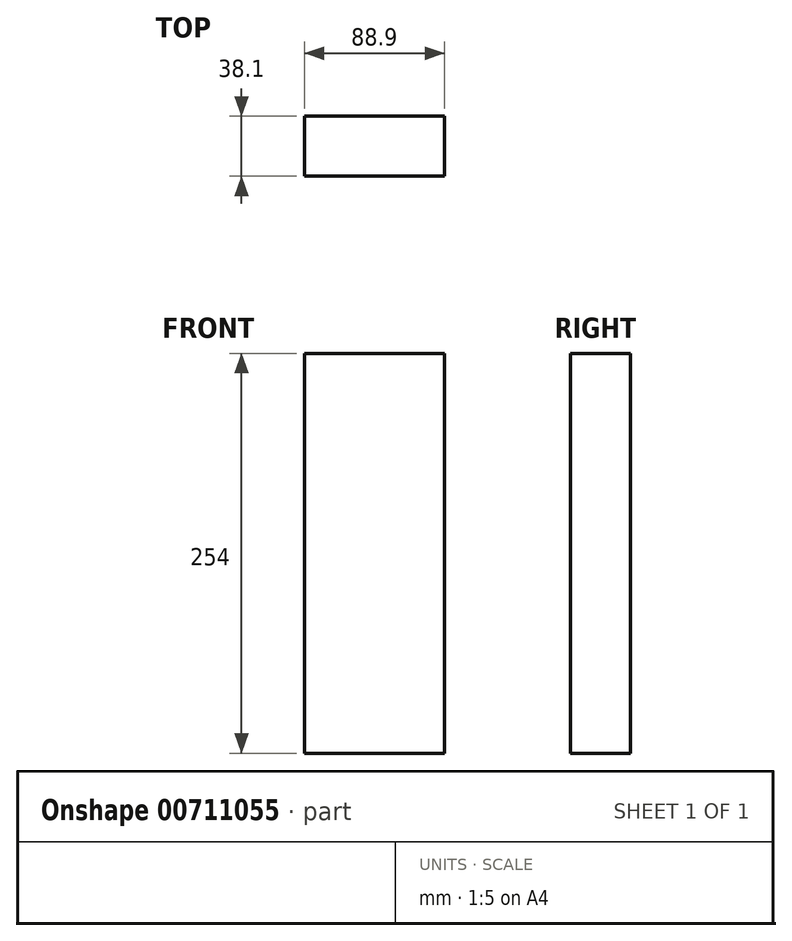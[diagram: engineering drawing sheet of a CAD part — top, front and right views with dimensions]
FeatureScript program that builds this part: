
annotation { "Feature Type Name" : "Feature", "Feature Type Description" : "" }
export const myFeature = defineFeature(function(context is Context, id is Id, definition is map)
    precondition{}
    {
        {
            var Q0;
            Q0=qCreatedBy(makeId("Top.planeOp"),FACE);
            var sketch = newSketch(context, id + "F0", { "sketchPlane" : qUnion([Q0])});
            skLineSegment(sketch, "E0.bottom", {"start": v(47.99, 19.05) * mm, "end": v(-40.91, 19.05) * mm});
            skLineSegment(sketch, "E0.top", {"start": v(47.99, -19.05) * mm, "end": v(-40.91, -19.05) * mm});
            skLineSegment(sketch, "E0.left", {"start": v(47.99, 19.05) * mm, "end": v(47.99, -19.05) * mm});
            skLineSegment(sketch, "E0.right", {"start": v(-40.91, 19.05) * mm, "end": v(-40.91, -19.05) * mm});
            skPoint(sketch, "E0.middle", {"position": v(3.54, 0) * mm});
            skSolve(sketch);
        }
        {
            var Q0;
            Q0=qSketchRegion(id+"F0",true);
            extrude(context, id + "F1", {"entities" : qUnion([Q0]), "depth" : 254 * mm, "offsetDistance" : 25.4 * mm});
        }
    });
